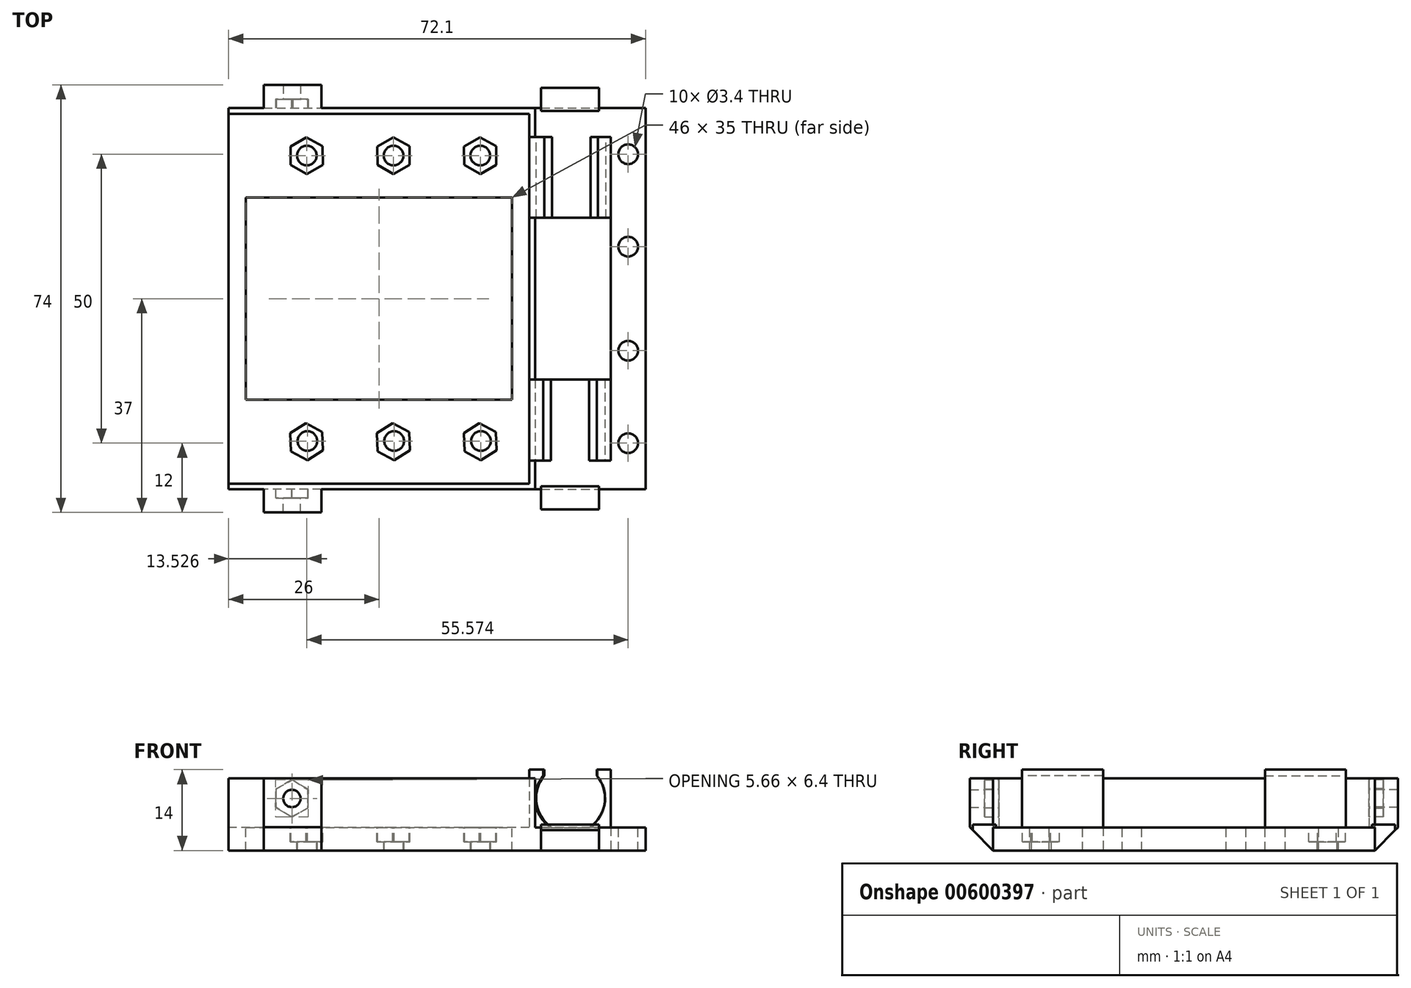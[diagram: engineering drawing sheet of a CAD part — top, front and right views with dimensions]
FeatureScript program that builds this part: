
annotation { "Feature Type Name" : "Feature", "Feature Type Description" : "" }
export const myFeature = defineFeature(function(context is Context, id is Id, definition is map)
    precondition{}
    {
        {
            var Q0;
            Q0=qCreatedBy(makeId("Top.planeOp"),FACE);
            var sketch = newSketch(context, id + "F0", { "sketchPlane" : qUnion([Q0])});
            skLineSegment(sketch, "E0.bottom", {"start": v(-26.5, 33) * mm, "end": v(26.5, 33) * mm});
            skLineSegment(sketch, "E0.top", {"start": v(-26.5, -33) * mm, "end": v(26.5, -33) * mm});
            skLineSegment(sketch, "E0.left", {"start": v(-26.5, 33) * mm, "end": v(-26.5, -33) * mm});
            skLineSegment(sketch, "E0.right", {"start": v(26.5, 33) * mm, "end": v(26.5, -33) * mm});
            skPoint(sketch, "E0.middle", {"position": v(0, 0) * mm});
            skSolve(sketch);
        }
        {
            var Q0;
            Q0=qSketchRegion(id+"F0",true);
            extrude(context, id + "F1", {"entities" : qUnion([Q0]), "depth" : 12.5 * mm});
        }
        {
            var Q0;
            Q0=makeQuery(id+"F1.opExtrude","SWEPT_FACE",FACE,{"disambiguationData":[OSD([sQuery(id+"F0.wireOp",EDGE,"E0.left")])]});
            var sketch = newSketch(context, id + "F2", { "sketchPlane" : qUnion([Q0])});
            skLineSegment(sketch, "E1.bottom", {"start": v(-32, 12.5) * mm, "end": v(32, 12.5) * mm});
            skLineSegment(sketch, "E1.top", {"start": v(-32, 4) * mm, "end": v(32, 4) * mm});
            skLineSegment(sketch, "E1.left", {"start": v(-32, 12.5) * mm, "end": v(-32, 4) * mm});
            skLineSegment(sketch, "E1.right", {"start": v(32, 12.5) * mm, "end": v(32, 4) * mm});
            skSolve(sketch);
        }
        {
            var Q0;
            Q0=qSketchRegion(id+"F2",true);
            extrude(context, id + "F3", {"entities" : qUnion([Q0]), "operationType" : NewBodyOperationType.REMOVE, "oppositeDirection" : true, "depth" : 52 * mm});
        }
        {
            var Q0;
            Q0=makeQuery(id+"F3.boolean.opBoolean","COPY",FACE,{"derivedFrom":makeQuery(id+"F3.opExtrude","SWEPT_FACE",FACE,{"disambiguationData":[OSD([sQuery(id+"F2.wireOp",EDGE,"E1.top")])]})});
            var sketch = newSketch(context, id + "F4", { "sketchPlane" : qUnion([Q0])});
            skLineSegment(sketch, "E2.bottom", {"start": v(-23.5, 17.5) * mm, "end": v(22.5, 17.5) * mm});
            skLineSegment(sketch, "E2.top", {"start": v(-23.5, -17.5) * mm, "end": v(22.5, -17.5) * mm});
            skLineSegment(sketch, "E2.left", {"start": v(-23.5, 17.5) * mm, "end": v(-23.5, -17.5) * mm});
            skLineSegment(sketch, "E2.right", {"start": v(22.5, 17.5) * mm, "end": v(22.5, -17.5) * mm});
            skSolve(sketch);
        }
        {
            var Q0;
            Q0=qSketchRegion(id+"F4",true);
            extrude(context, id + "F5", {"entities" : qUnion([Q0]), "operationType" : NewBodyOperationType.REMOVE, "oppositeDirection" : true, "depth" : 5 * mm, "offsetDistance" : 25 * mm});
        }
        {
            var Q0;
            Q0=makeQuery(id+"F1.opExtrude","SWEPT_FACE",FACE,{"disambiguationData":[OSD([sQuery(id+"F0.wireOp",EDGE,"E0.right")])]});
            var sketch = newSketch(context, id + "F6", { "sketchPlane" : qUnion([Q0])});
            skLineSegment(sketch, "E3.bottom", {"start": v(-28, 12.5) * mm, "end": v(-14, 12.5) * mm});
            skLineSegment(sketch, "E3.top", {"start": v(-28, 0) * mm, "end": v(-14, 0) * mm});
            skLineSegment(sketch, "E3.left", {"start": v(-28, 12.5) * mm, "end": v(-28, 0) * mm});
            skLineSegment(sketch, "E3.right", {"start": v(-14, 12.5) * mm, "end": v(-14, 0) * mm});
            skSolve(sketch);
        }
        {
            var Q0;
            Q0=qSketchRegion(id+"F6",true);
            extrude(context, id + "F7", {"entities" : qUnion([Q0]), "operationType" : NewBodyOperationType.REMOVE, "oppositeDirection" : true, "depth" : 1 * mm});
        }
        {
            var Q0;
            Q0=makeQuery(id+"F7.boolean.opBoolean","COPY",FACE,{"derivedFrom":makeQuery(id+"F7.opExtrude","CAP_FACE",FACE,{"disambiguationData":[OSD([sQuery(id+"F6.wireOp",EDGE,"E3.bottom"),sQuery(id+"F6.wireOp",EDGE,"E3.top"),sQuery(id+"F6.wireOp",EDGE,"E3.left"),sQuery(id+"F6.wireOp",EDGE,"E3.right")])],"isStart":false})});
            var sketch = newSketch(context, id + "F8", { "sketchPlane" : qUnion([Q0])});
            skLineSegment(sketch, "E4.bottom", {"start": v(-14, 0) * mm, "end": v(-28, 0) * mm});
            skLineSegment(sketch, "E4.top", {"start": v(-14, 14) * mm, "end": v(-28, 14) * mm});
            skLineSegment(sketch, "E4.left", {"start": v(-14, 0) * mm, "end": v(-14, 14) * mm});
            skLineSegment(sketch, "E4.right", {"start": v(-28, 0) * mm, "end": v(-28, 14) * mm});
            skSolve(sketch);
        }
        {
            var Q0;
            Q0=qSketchRegion(id+"F8",true);
            extrude(context, id + "F9", {"entities" : qUnion([Q0]), "operationType" : NewBodyOperationType.ADD, "depth" : 14.1 * mm});
        }
        {
            var Q0;
            Q0=makeQuery(id+"F9.opExtrude","SWEPT_FACE",FACE,{"disambiguationData":[OSD([sQuery(id+"F8.wireOp",EDGE,"E4.right")])]});
            var sketch = newSketch(context, id + "F10", { "sketchPlane" : qUnion([Q0])});
            skArc(sketch, "E5", {"start": v(27.89, 12.91) * mm, "mid": v(26.56, 8.16) * mm, "end": v(29.21, 4) * mm});
            skLineSegment(sketch, "E6", {"start": v(27.89, 14) * mm, "end": v(27.89, 12.91) * mm});
            skLineSegment(sketch, "E7", {"start": v(37.2, 12.91) * mm, "end": v(37.2, 14) * mm});
            skLineSegment(sketch, "E8", {"start": v(27.89, 14) * mm, "end": v(37.2, 14) * mm});
            skLineSegment(sketch, "E9", {"start": v(29.21, 4) * mm, "end": v(35.88, 4) * mm});
            skArc(sketch, "E10.trimOffspring", {"start": v(35.88, 4) * mm, "mid": v(38.53, 8.16) * mm, "end": v(37.2, 12.91) * mm});
            skSolve(sketch);
        }
        {
            var Q0;
            Q0=qSketchRegion(id+"F10",true);
            extrude(context, id + "F11", {"entities" : qUnion([Q0]), "operationType" : NewBodyOperationType.REMOVE, "oppositeDirection" : true, "depth" : 14 * mm});
        }
        {
            var Q0;
            {var subQ0=sQuery(id+"F0.wireOp",EDGE,"E0.bottom");var subQ1=sQuery(id+"F0.wireOp",EDGE,"E0.right");Q0=makeQuery(id+"F7.boolean.opBoolean","SPLIT",FACE,{"disambiguationData":[TD([makeQuery(id+"F1.opExtrude","SWEPT_FACE",FACE,{"disambiguationData":[OSD([subQ0])]})])],"derivedFrom":makeQuery(id+"F1.opExtrude","SWEPT_FACE",FACE,{"disambiguationData":[OSD([subQ1])]})});}
            var sketch = newSketch(context, id + "F12", { "sketchPlane" : qUnion([Q0])});
            skLineSegment(sketch, "E11.bottom", {"start": v(28, 0) * mm, "end": v(14, 0) * mm});
            skLineSegment(sketch, "E11.top", {"start": v(28, 14) * mm, "end": v(14, 14) * mm});
            skLineSegment(sketch, "E11.left", {"start": v(28, 0) * mm, "end": v(28, 14) * mm});
            skLineSegment(sketch, "E11.right", {"start": v(14, 0) * mm, "end": v(14, 14) * mm});
            skSolve(sketch);
        }
        {
            var Q0;
            Q0=qSketchRegion(id+"F12",true);
            var Q1;
            {var subQ3=sQuery(id+"F2.wireOp",EDGE,"E1.right");var subQ4=sQuery(id+"F2.wireOp",EDGE,"E1.top");var subQ7=sQuery(id+"F2.wireOp",EDGE,"E1.left");var subQ8=makeQuery(id+"F3.boolean.opBoolean","COPY",FACE,{"derivedFrom":makeQuery(id+"F3.opExtrude","CAP_FACE",FACE,{"disambiguationData":[OSD([sQuery(id+"F2.wireOp",EDGE,"E1.bottom"),subQ4,subQ7,subQ3])],"isStart":false})});Q1=makeQuery(id+"F9.boolean.opBoolean","MERGE",FACE,{"derivedFrom":[makeQuery(id+"F7.boolean.opBoolean","SPLIT",FACE,{"disambiguationData":[TD([makeQuery(id+"F3.boolean.opBoolean","COPY",FACE,{"derivedFrom":makeQuery(id+"F3.opExtrude","SWEPT_FACE",FACE,{"disambiguationData":[OSD([subQ7])]})})])],"derivedFrom":subQ8}),makeQuery(id+"F7.boolean.opBoolean","SPLIT",FACE,{"disambiguationData":[TD([makeQuery(id+"F3.boolean.opBoolean","COPY",FACE,{"derivedFrom":makeQuery(id+"F3.opExtrude","SWEPT_FACE",FACE,{"disambiguationData":[OSD([subQ3])]})})])],"derivedFrom":subQ8}),makeQuery(id+"F9.opExtrude","CAP_FACE",FACE,{"disambiguationData":[OSD([sQuery(id+"F8.wireOp",EDGE,"E4.bottom"),sQuery(id+"F8.wireOp",EDGE,"E4.top"),sQuery(id+"F8.wireOp",EDGE,"E4.left"),sQuery(id+"F8.wireOp",EDGE,"E4.right")])],"isStart":true})]});}
            extrude(context, id + "F13", {"entities" : qUnion([Q0]), "operationType" : NewBodyOperationType.ADD, "endBound" : BoundingType.UP_TO_SURFACE, "oppositeDirection" : true, "endBoundEntityFace" : qUnion([Q1]), "depth" : 25 * mm, "hasSecondDirection" : true, "secondDirectionOppositeDirection" : false, "secondDirectionDepth" : 13.1 * mm});
        }
        {
            var Q0;
            Q0=makeQuery(id+"F13.opExtrude","SWEPT_FACE",FACE,{"disambiguationData":[OSD([sQuery(id+"F12.wireOp",EDGE,"E11.left")])]});
            var sketch = newSketch(context, id + "F14", { "sketchPlane" : qUnion([Q0])});
            skArc(sketch, "E12", {"start": v(-37.37, 12.94) * mm, "mid": v(-38.72, 8.18) * mm, "end": v(-36.07, 4) * mm});
            skLineSegment(sketch, "E13", {"start": v(-36.07, 4) * mm, "end": v(-29.4, 4) * mm});
            skLineSegment(sketch, "E14", {"start": v(-37.37, 14) * mm, "end": v(-37.37, 12.94) * mm});
            skLineSegment(sketch, "E15", {"start": v(-28.1, 12.94) * mm, "end": v(-28.1, 14) * mm});
            skArc(sketch, "E16.trimOffspring", {"start": v(-29.4, 4) * mm, "mid": v(-26.75, 8.18) * mm, "end": v(-28.1, 12.94) * mm});
            skLineSegment(sketch, "E17", {"start": v(-37.37, 14) * mm, "end": v(-28.1, 14) * mm});
            skSolve(sketch);
        }
        {
            var Q0;
            Q0=qSketchRegion(id+"F14",true);
            extrude(context, id + "F15", {"entities" : qUnion([Q0]), "operationType" : NewBodyOperationType.REMOVE, "oppositeDirection" : true, "depth" : 14 * mm});
        }
        {
            var Q0;
            {var subQ0=sQuery(id+"F0.wireOp",EDGE,"E0.right");var subQ2=sQuery(id+"F0.wireOp",EDGE,"E0.top");Q0=makeQuery(id+"F7.boolean.opBoolean","SPLIT",FACE,{"disambiguationData":[TD([makeQuery(id+"F1.opExtrude","SWEPT_FACE",FACE,{"disambiguationData":[OSD([subQ2])]})])],"derivedFrom":makeQuery(id+"F1.opExtrude","SWEPT_FACE",FACE,{"disambiguationData":[OSD([subQ0])]})});}
            var sketch = newSketch(context, id + "F16", { "sketchPlane" : qUnion([Q0])});
            skLineSegment(sketch, "E18.bottom", {"start": v(-33, 4) * mm, "end": v(-28, 4) * mm});
            skLineSegment(sketch, "E18.top", {"start": v(-33, 0) * mm, "end": v(-28, 0) * mm});
            skLineSegment(sketch, "E18.left", {"start": v(-33, 4) * mm, "end": v(-33, 0) * mm});
            skLineSegment(sketch, "E18.right", {"start": v(-28, 4) * mm, "end": v(-28, 0) * mm});
            skSolve(sketch);
        }
        {
            var Q0;
            Q0=qSketchRegion(id+"F16",true);
            var Q1;
            Q1=makeQuery(id+"F9.opExtrude","CAP_FACE",FACE,{"disambiguationData":[OSD([sQuery(id+"F8.wireOp",EDGE,"E4.bottom"),sQuery(id+"F8.wireOp",EDGE,"E4.top"),sQuery(id+"F8.wireOp",EDGE,"E4.left"),sQuery(id+"F8.wireOp",EDGE,"E4.right")])],"isStart":false});
            extrude(context, id + "F17", {"entities" : qUnion([Q0]), "operationType" : NewBodyOperationType.ADD, "endBound" : BoundingType.UP_TO_SURFACE, "endBoundEntityFace" : qUnion([Q1]), "depth" : 25 * mm});
        }
        {
            var Q0;
            {var subQ0=sQuery(id+"F0.wireOp",EDGE,"E0.right");var subQ3=sQuery(id+"F0.wireOp",EDGE,"E0.bottom");var subQ6=makeQuery(id+"F1.opExtrude","SWEPT_FACE",FACE,{"disambiguationData":[OSD([subQ3])]});Q0=makeQuery(id+"F13.boolean.opBoolean","SPLIT",FACE,{"disambiguationData":[TD([subQ6])],"derivedFrom":makeQuery(id+"F7.boolean.opBoolean","SPLIT",FACE,{"disambiguationData":[TD([subQ6])],"derivedFrom":makeQuery(id+"F1.opExtrude","SWEPT_FACE",FACE,{"disambiguationData":[OSD([subQ0])]})})});}
            var sketch = newSketch(context, id + "F18", { "sketchPlane" : qUnion([Q0])});
            skLineSegment(sketch, "E19.bottom", {"start": v(28, 4) * mm, "end": v(33, 4) * mm});
            skLineSegment(sketch, "E19.top", {"start": v(28, 0) * mm, "end": v(33, 0) * mm});
            skLineSegment(sketch, "E19.left", {"start": v(28, 4) * mm, "end": v(28, 0) * mm});
            skLineSegment(sketch, "E19.right", {"start": v(33, 4) * mm, "end": v(33, 0) * mm});
            skSolve(sketch);
        }
        {
            var Q0;
            Q0=qSketchRegion(id+"F18",true);
            var Q1;
            Q1=makeQuery(id+"F13.opExtrude","CAP_FACE",FACE,{"disambiguationData":[OSD([sQuery(id+"F12.wireOp",EDGE,"E11.bottom"),sQuery(id+"F12.wireOp",EDGE,"E11.top"),sQuery(id+"F12.wireOp",EDGE,"E11.left"),sQuery(id+"F12.wireOp",EDGE,"E11.right")])],"isStart":true});
            extrude(context, id + "F19", {"entities" : qUnion([Q0]), "operationType" : NewBodyOperationType.ADD, "endBound" : BoundingType.UP_TO_SURFACE, "endBoundEntityFace" : qUnion([Q1]), "depth" : 25 * mm});
        }
        {
            var Q0;
            {var subQ0=sQuery(id+"F8.wireOp",EDGE,"E4.right");var subQ1=sQuery(id+"F8.wireOp",EDGE,"E4.left");var subQ2=sQuery(id+"F8.wireOp",EDGE,"E4.top");var subQ3=sQuery(id+"F8.wireOp",EDGE,"E4.bottom");Q0=makeQuery(id+"F17.boolean.opBoolean","MERGE",FACE,{"derivedFrom":[makeQuery(id+"F9.opExtrude","CAP_FACE",FACE,{"disambiguationData":[OSD([subQ3,subQ2,subQ1,subQ0])],"isStart":false}),makeQuery(id+"F17.opExtrude","CAP_FACE",FACE,{"disambiguationData":[OSD([subQ3,subQ2,subQ1,subQ0])],"isStart":false})]});}
            var sketch = newSketch(context, id + "F20", { "sketchPlane" : qUnion([Q0])});
            skLineSegment(sketch, "E20.bottom", {"start": v(-33, 4) * mm, "end": v(33, 4) * mm});
            skLineSegment(sketch, "E20.top", {"start": v(-33, 0) * mm, "end": v(33, 0) * mm});
            skLineSegment(sketch, "E20.left", {"start": v(-33, 4) * mm, "end": v(-33, 0) * mm});
            skLineSegment(sketch, "E20.right", {"start": v(33, 4) * mm, "end": v(33, 0) * mm});
            skSolve(sketch);
        }
        {
            var Q0;
            Q0=qSketchRegion(id+"F20",true);
            extrude(context, id + "F21", {"entities" : qUnion([Q0]), "operationType" : NewBodyOperationType.ADD, "depth" : 6 * mm});
        }
        {
            var Q0;
            Q0=makeQuery(id+"F21.boolean.opBoolean","MERGE",FACE,{"derivedFrom":[makeQuery(id+"F17.boolean.opBoolean","MERGE",FACE,{"derivedFrom":[makeQuery(id+"F1.opExtrude","SWEPT_FACE",FACE,{"disambiguationData":[OSD([sQuery(id+"F0.wireOp",EDGE,"E0.top")])]}),makeQuery(id+"F17.opExtrude","SWEPT_FACE",FACE,{"disambiguationData":[OSD([sQuery(id+"F16.wireOp",EDGE,"E18.left")])]})]}),makeQuery(id+"F21.opExtrude","SWEPT_FACE",FACE,{"disambiguationData":[OSD([sQuery(id+"F20.wireOp",EDGE,"E20.left")])]})]});
            var sketch = newSketch(context, id + "F22", { "sketchPlane" : qUnion([Q0])});
            skLineSegment(sketch, "E21.bottom", {"start": v(37.55, 0) * mm, "end": v(27.55, 0) * mm});
            skLineSegment(sketch, "E21.top", {"start": v(37.55, 4.5) * mm, "end": v(27.55, 4.5) * mm});
            skLineSegment(sketch, "E21.left", {"start": v(37.55, 0) * mm, "end": v(37.55, 4.5) * mm});
            skLineSegment(sketch, "E21.right", {"start": v(27.55, 0) * mm, "end": v(27.55, 4.5) * mm});
            skSolve(sketch);
        }
        {
            var Q0;
            Q0=qSketchRegion(id+"F22",true);
            extrude(context, id + "F23", {"entities" : qUnion([Q0]), "operationType" : NewBodyOperationType.ADD, "oppositeDirection" : true, "depth" : .5 * mm, "hasSecondDirection" : true, "secondDirectionOppositeDirection" : false, "secondDirectionDepth" : 3.5 * mm});
        }
        {
            var Q0;
            Q0=makeQuery(id+"F23.opExtrude","SWEPT_FACE",FACE,{"disambiguationData":[OSD([sQuery(id+"F22.wireOp",EDGE,"E21.left")])]});
            var sketch = newSketch(context, id + "F24", { "sketchPlane" : qUnion([Q0])});
            skLineSegment(sketch, "E22", {"start": v(-33, 0) * mm, "end": v(-36.5, 3.5) * mm});
            skLineSegment(sketch, "E23", {"start": v(-36.5, 3.5) * mm, "end": v(-36.5, 0) * mm});
            skLineSegment(sketch, "E24", {"start": v(-36.5, 0) * mm, "end": v(-33, 0) * mm});
            skSolve(sketch);
        }
        {
            var Q0;
            Q0=qSketchRegion(id+"F24",true);
            extrude(context, id + "F25", {"entities" : qUnion([Q0]), "operationType" : NewBodyOperationType.REMOVE, "oppositeDirection" : true, "depth" : 10 * mm});
        }
        {
            var Q0;
            {var subQ1=sQuery(id+"F0.wireOp",EDGE,"E0.left");var subQ2=sQuery(id+"F0.wireOp",EDGE,"E0.top");Q0=makeQuery(id+"F23.boolean.opBoolean","SPLIT",FACE,{"disambiguationData":[TD([makeQuery(id+"F1.opExtrude","SWEPT_FACE",FACE,{"disambiguationData":[OSD([subQ1])]})])],"derivedFrom":makeQuery(id+"F21.boolean.opBoolean","MERGE",FACE,{"derivedFrom":[makeQuery(id+"F17.boolean.opBoolean","MERGE",FACE,{"derivedFrom":[makeQuery(id+"F1.opExtrude","SWEPT_FACE",FACE,{"disambiguationData":[OSD([subQ2])]}),makeQuery(id+"F17.opExtrude","SWEPT_FACE",FACE,{"disambiguationData":[OSD([sQuery(id+"F16.wireOp",EDGE,"E18.left")])]})]}),makeQuery(id+"F21.opExtrude","SWEPT_FACE",FACE,{"disambiguationData":[OSD([sQuery(id+"F20.wireOp",EDGE,"E20.left")])]})]})});}
            var sketch = newSketch(context, id + "F26", { "sketchPlane" : qUnion([Q0])});
            skLineSegment(sketch, "E25.bottom", {"start": v(-20.45, 12.5) * mm, "end": v(-10.45, 12.5) * mm});
            skLineSegment(sketch, "E25.top", {"start": v(-20.45, 0) * mm, "end": v(-10.45, 0) * mm});
            skLineSegment(sketch, "E25.left", {"start": v(-20.45, 12.5) * mm, "end": v(-20.45, 0) * mm});
            skLineSegment(sketch, "E25.right", {"start": v(-10.45, 12.5) * mm, "end": v(-10.45, 0) * mm});
            skSolve(sketch);
        }
        {
            var Q0;
            Q0=qSketchRegion(id+"F26",true);
            extrude(context, id + "F27", {"entities" : qUnion([Q0]), "operationType" : NewBodyOperationType.ADD, "depth" : 4 * mm});
        }
        {
            var Q0;
            Q0=makeQuery(id+"F27.opExtrude","SWEPT_FACE",FACE,{"disambiguationData":[OSD([sQuery(id+"F26.wireOp",EDGE,"E25.left")])]});
            var sketch = newSketch(context, id + "F28", { "sketchPlane" : qUnion([Q0])});
            skLineSegment(sketch, "E26", {"start": v(37, 0) * mm, "end": v(37, 4.04) * mm});
            skLineSegment(sketch, "E27", {"start": v(37, 4.04) * mm, "end": v(33, 0) * mm});
            skLineSegment(sketch, "E28", {"start": v(33, 0) * mm, "end": v(37, 0) * mm});
            skSolve(sketch);
        }
        {
            var Q0;
            Q0=qSketchRegion(id+"F28",true);
            var Q1;
            Q1=makeQuery(id+"F27.opExtrude","SWEPT_FACE",FACE,{"disambiguationData":[OSD([sQuery(id+"F26.wireOp",EDGE,"E25.right")])]});
            extrude(context, id + "F29", {"entities" : qUnion([Q0]), "operationType" : NewBodyOperationType.REMOVE, "endBound" : BoundingType.UP_TO_SURFACE, "oppositeDirection" : true, "endBoundEntityFace" : qUnion([Q1]), "depth" : 25 * mm});
        }
        {
            var Q0;
            Q0=makeQuery(id+"F21.boolean.opBoolean","MERGE",FACE,{"derivedFrom":[makeQuery(id+"F19.boolean.opBoolean","MERGE",FACE,{"derivedFrom":[makeQuery(id+"F1.opExtrude","SWEPT_FACE",FACE,{"disambiguationData":[OSD([sQuery(id+"F0.wireOp",EDGE,"E0.bottom")])]}),makeQuery(id+"F19.opExtrude","SWEPT_FACE",FACE,{"disambiguationData":[OSD([sQuery(id+"F18.wireOp",EDGE,"E19.right")])]})]}),makeQuery(id+"F21.opExtrude","SWEPT_FACE",FACE,{"disambiguationData":[OSD([sQuery(id+"F20.wireOp",EDGE,"E20.right")])]})]});
            var sketch = newSketch(context, id + "F30", { "sketchPlane" : qUnion([Q0])});
            skLineSegment(sketch, "E29.bottom", {"start": v(-27.55, 0) * mm, "end": v(-37.55, 0) * mm});
            skLineSegment(sketch, "E29.top", {"start": v(-27.55, 4.5) * mm, "end": v(-37.55, 4.5) * mm});
            skLineSegment(sketch, "E29.left", {"start": v(-27.55, 0) * mm, "end": v(-27.55, 4.5) * mm});
            skLineSegment(sketch, "E29.right", {"start": v(-37.55, 0) * mm, "end": v(-37.55, 4.5) * mm});
            skSolve(sketch);
        }
        {
            var Q0;
            Q0=qSketchRegion(id+"F30",true);
            extrude(context, id + "F31", {"entities" : qUnion([Q0]), "operationType" : NewBodyOperationType.ADD, "oppositeDirection" : true, "depth" : 0.5 * mm, "hasSecondDirection" : true, "secondDirectionOppositeDirection" : false, "secondDirectionDepth" : 3.5 * mm});
        }
        {
            var Q0;
            Q0=makeQuery(id+"F31.opExtrude","SWEPT_FACE",FACE,{"disambiguationData":[OSD([sQuery(id+"F30.wireOp",EDGE,"E29.right")])]});
            var sketch = newSketch(context, id + "F32", { "sketchPlane" : qUnion([Q0])});
            skLineSegment(sketch, "E30", {"start": v(33, 0) * mm, "end": v(36.5, 3.5) * mm});
            skLineSegment(sketch, "E31", {"start": v(36.5, 3.5) * mm, "end": v(36.5, 0) * mm});
            skLineSegment(sketch, "E32", {"start": v(36.5, 0) * mm, "end": v(33, 0) * mm});
            skSolve(sketch);
        }
        {
            var Q0;
            Q0=qSketchRegion(id+"F32",true);
            var Q1;
            Q1=makeQuery(id+"F31.opExtrude","SWEPT_FACE",FACE,{"disambiguationData":[OSD([sQuery(id+"F30.wireOp",EDGE,"E29.left")])]});
            extrude(context, id + "F33", {"entities" : qUnion([Q0]), "operationType" : NewBodyOperationType.REMOVE, "endBound" : BoundingType.UP_TO_SURFACE, "oppositeDirection" : true, "endBoundEntityFace" : qUnion([Q1]), "depth" : 25 * mm});
        }
        {
            var Q0;
            {var subQ1=sQuery(id+"F0.wireOp",EDGE,"E0.left");var subQ3=sQuery(id+"F0.wireOp",EDGE,"E0.bottom");Q0=makeQuery(id+"F31.boolean.opBoolean","SPLIT",FACE,{"disambiguationData":[TD([makeQuery(id+"F1.opExtrude","SWEPT_FACE",FACE,{"disambiguationData":[OSD([subQ1])]})])],"derivedFrom":makeQuery(id+"F21.boolean.opBoolean","MERGE",FACE,{"derivedFrom":[makeQuery(id+"F19.boolean.opBoolean","MERGE",FACE,{"derivedFrom":[makeQuery(id+"F1.opExtrude","SWEPT_FACE",FACE,{"disambiguationData":[OSD([subQ3])]}),makeQuery(id+"F19.opExtrude","SWEPT_FACE",FACE,{"disambiguationData":[OSD([sQuery(id+"F18.wireOp",EDGE,"E19.right")])]})]}),makeQuery(id+"F21.opExtrude","SWEPT_FACE",FACE,{"disambiguationData":[OSD([sQuery(id+"F20.wireOp",EDGE,"E20.right")])]})]})});}
            var sketch = newSketch(context, id + "F34", { "sketchPlane" : qUnion([Q0])});
            skLineSegment(sketch, "E33.bottom", {"start": v(10.45, 12.5) * mm, "end": v(20.45, 12.5) * mm});
            skLineSegment(sketch, "E33.top", {"start": v(10.45, 0) * mm, "end": v(20.45, 0) * mm});
            skLineSegment(sketch, "E33.left", {"start": v(10.45, 12.5) * mm, "end": v(10.45, 0) * mm});
            skLineSegment(sketch, "E33.right", {"start": v(20.45, 12.5) * mm, "end": v(20.45, 0) * mm});
            skSolve(sketch);
        }
        {
            var Q0;
            Q0=qSketchRegion(id+"F34",true);
            extrude(context, id + "F35", {"entities" : qUnion([Q0]), "operationType" : NewBodyOperationType.ADD, "depth" : 4 * mm});
        }
        {
            var Q0;
            Q0=makeQuery(id+"F35.opExtrude","SWEPT_FACE",FACE,{"disambiguationData":[OSD([sQuery(id+"F34.wireOp",EDGE,"E33.left")])]});
            var sketch = newSketch(context, id + "F36", { "sketchPlane" : qUnion([Q0])});
            skLineSegment(sketch, "E34", {"start": v(33, 0) * mm, "end": v(37, 4) * mm});
            skLineSegment(sketch, "E35", {"start": v(37, 4) * mm, "end": v(37, 0) * mm});
            skLineSegment(sketch, "E36", {"start": v(37, 0) * mm, "end": v(33, 0) * mm});
            skSolve(sketch);
        }
        {
            var Q0;
            Q0=qSketchRegion(id+"F36",true);
            var Q1;
            Q1=makeQuery(id+"F35.opExtrude","SWEPT_FACE",FACE,{"disambiguationData":[OSD([sQuery(id+"F34.wireOp",EDGE,"E33.right")])]});
            extrude(context, id + "F37", {"entities" : qUnion([Q0]), "operationType" : NewBodyOperationType.REMOVE, "endBound" : BoundingType.UP_TO_SURFACE, "oppositeDirection" : true, "endBoundEntityFace" : qUnion([Q1]), "depth" : 25 * mm});
        }
        {
            var Q0;
            Q0=makeQuery(id+"F3.boolean.opBoolean","COPY",FACE,{"derivedFrom":makeQuery(id+"F3.opExtrude","SWEPT_FACE",FACE,{"disambiguationData":[OSD([sQuery(id+"F2.wireOp",EDGE,"E1.right")])]})});
            var sketch = newSketch(context, id + "F38", { "sketchPlane" : qUnion([Q0])});
            skCircle(sketch, "E37.cCircle", {"center": v(15.55, 9) * mm, "radius": 2.77 * mm, "construction": true});
            skLineSegment(sketch, "E37.0", {"start": v(12.8, 10.62) * mm, "end": v(15.57, 12.2) * mm});
            skLineSegment(sketch, "E37.1", {"start": v(15.57, 12.2) * mm, "end": v(18.33, 10.58) * mm});
            skLineSegment(sketch, "E37.2", {"start": v(18.33, 10.58) * mm, "end": v(18.3, 7.38) * mm});
            skLineSegment(sketch, "E37.3", {"start": v(18.3, 7.38) * mm, "end": v(15.53, 5.8) * mm});
            skLineSegment(sketch, "E37.4", {"start": v(15.53, 5.8) * mm, "end": v(12.77, 7.42) * mm});
            skLineSegment(sketch, "E37.5", {"start": v(12.77, 7.42) * mm, "end": v(12.8, 10.62) * mm});
            skPoint(sketch, "E37.0.midPoint", {"position": v(14.18, 11.41) * mm});
            skSolve(sketch);
        }
        {
            var Q0;
            Q0=qSketchRegion(id+"F38",true);
            extrude(context, id + "F39", {"entities" : qUnion([Q0]), "operationType" : NewBodyOperationType.REMOVE, "oppositeDirection" : true, "depth" : 2.5 * mm});
        }
        {
            var Q0;
            Q0=makeQuery(id+"F3.boolean.opBoolean","COPY",FACE,{"derivedFrom":makeQuery(id+"F3.opExtrude","SWEPT_FACE",FACE,{"disambiguationData":[OSD([sQuery(id+"F2.wireOp",EDGE,"E1.right")])]})});
            var sketch = newSketch(context, id + "F40", { "sketchPlane" : qUnion([Q0])});
            skCircle(sketch, "E38", {"center": v(15.55, 9) * mm, "radius": 1.5 * mm});
            skSolve(sketch);
        }
        {
            var Q0;
            Q0=qSketchRegion(id+"F40",true);
            extrude(context, id + "F41", {"entities" : qUnion([Q0]), "operationType" : NewBodyOperationType.REMOVE, "oppositeDirection" : true, "depth" : 6 * mm});
        }
        {
            var Q0;
            Q0=makeQuery(id+"F3.boolean.opBoolean","COPY",FACE,{"derivedFrom":makeQuery(id+"F3.opExtrude","SWEPT_FACE",FACE,{"disambiguationData":[OSD([sQuery(id+"F2.wireOp",EDGE,"E1.left")])]})});
            var sketch = newSketch(context, id + "F42", { "sketchPlane" : qUnion([Q0])});
            skCircle(sketch, "E39.cCircle", {"center": v(-15.55, 9) * mm, "radius": 2.77 * mm, "construction": true});
            skLineSegment(sketch, "E39.0", {"start": v(-12.84, 7.3) * mm, "end": v(-15.67, 5.8) * mm});
            skLineSegment(sketch, "E39.1", {"start": v(-15.67, 5.8) * mm, "end": v(-18.38, 7.5) * mm});
            skLineSegment(sketch, "E39.2", {"start": v(-18.38, 7.5) * mm, "end": v(-18.26, 10.7) * mm});
            skLineSegment(sketch, "E39.3", {"start": v(-18.26, 10.7) * mm, "end": v(-15.43, 12.2) * mm});
            skLineSegment(sketch, "E39.4", {"start": v(-15.43, 12.2) * mm, "end": v(-12.72, 10.5) * mm});
            skLineSegment(sketch, "E39.5", {"start": v(-12.72, 10.5) * mm, "end": v(-12.84, 7.3) * mm});
            skPoint(sketch, "E39.0.midPoint", {"position": v(-14.25, 6.55) * mm});
            skSolve(sketch);
        }
        {
            var Q0;
            Q0=qSketchRegion(id+"F42",true);
            extrude(context, id + "F43", {"entities" : qUnion([Q0]), "operationType" : NewBodyOperationType.REMOVE, "oppositeDirection" : true, "depth" : 2.5 * mm});
        }
        {
            var Q0;
            Q0=makeQuery(id+"F3.boolean.opBoolean","COPY",FACE,{"derivedFrom":makeQuery(id+"F3.opExtrude","SWEPT_FACE",FACE,{"disambiguationData":[OSD([sQuery(id+"F2.wireOp",EDGE,"E1.left")])]})});
            var sketch = newSketch(context, id + "F44", { "sketchPlane" : qUnion([Q0])});
            skCircle(sketch, "E40", {"center": v(-15.55, 9) * mm, "radius": 1.5 * mm});
            skSolve(sketch);
        }
        {
            var Q0;
            Q0=qSketchRegion(id+"F44",true);
            extrude(context, id + "F45", {"entities" : qUnion([Q0]), "operationType" : NewBodyOperationType.REMOVE, "oppositeDirection" : true, "depth" : 6 * mm});
        }
        {
            var Q0;
            Q0=makeQuery(id+"F21.boolean.opBoolean","MERGE",FACE,{"derivedFrom":[makeQuery(id+"F17.boolean.opBoolean","MERGE",FACE,{"derivedFrom":[makeQuery(id+"F11.boolean.opBoolean","COPY",FACE,{"derivedFrom":makeQuery(id+"F11.opExtrude","SWEPT_FACE",FACE,{"disambiguationData":[OSD([sQuery(id+"F10.wireOp",EDGE,"E9")])]})}),makeQuery(id+"F17.opExtrude","SWEPT_FACE",FACE,{"disambiguationData":[OSD([sQuery(id+"F16.wireOp",EDGE,"E18.bottom")])]})]}),makeQuery(id+"F19.boolean.opBoolean","MERGE",FACE,{"derivedFrom":[makeQuery(id+"F15.boolean.opBoolean","COPY",FACE,{"derivedFrom":makeQuery(id+"F15.opExtrude","SWEPT_FACE",FACE,{"disambiguationData":[OSD([sQuery(id+"F14.wireOp",EDGE,"E13")])]})}),makeQuery(id+"F19.opExtrude","SWEPT_FACE",FACE,{"disambiguationData":[OSD([sQuery(id+"F18.wireOp",EDGE,"E19.bottom")])]})]}),makeQuery(id+"F21.opExtrude","SWEPT_FACE",FACE,{"disambiguationData":[OSD([sQuery(id+"F20.wireOp",EDGE,"E20.bottom")])]})]});
            var sketch = newSketch(context, id + "F46", { "sketchPlane" : qUnion([Q0])});
            skCircle(sketch, "E41", {"center": v(42.6, -25) * mm, "radius": 1.7 * mm});
            skCircle(sketch, "E42", {"center": v(42.6, -9) * mm, "radius": 1.7 * mm});
            skCircle(sketch, "E43", {"center": v(42.6, 9) * mm, "radius": 1.7 * mm});
            skCircle(sketch, "E44", {"center": v(42.6, 25) * mm, "radius": 1.7 * mm});
            skSolve(sketch);
        }
        {
            var Q0;
            Q0=qSketchRegion(id+"F46",true);
            extrude(context, id + "F47", {"entities" : qUnion([Q0]), "operationType" : NewBodyOperationType.REMOVE, "oppositeDirection" : true, "depth" : 5 * mm});
        }
        {
            var Q0;
            Q0=makeQuery(id+"F3.boolean.opBoolean","COPY",FACE,{"derivedFrom":makeQuery(id+"F3.opExtrude","SWEPT_FACE",FACE,{"disambiguationData":[OSD([sQuery(id+"F2.wireOp",EDGE,"E1.top")])]})});
            var sketch = newSketch(context, id + "F48", { "sketchPlane" : qUnion([Q0])});
            skCircle(sketch, "E45.cCircle", {"center": v(-13, 24.75) * mm, "radius": 2.77 * mm, "construction": true});
            skLineSegment(sketch, "E45.0", {"start": v(-10.22, 23.17) * mm, "end": v(-12.97, 21.55) * mm});
            skLineSegment(sketch, "E45.1", {"start": v(-12.97, 21.55) * mm, "end": v(-15.76, 23.13) * mm});
            skLineSegment(sketch, "E45.2", {"start": v(-15.76, 23.13) * mm, "end": v(-15.78, 26.33) * mm});
            skLineSegment(sketch, "E45.3", {"start": v(-15.78, 26.33) * mm, "end": v(-13.03, 27.95) * mm});
            skLineSegment(sketch, "E45.4", {"start": v(-13.03, 27.95) * mm, "end": v(-10.24, 26.37) * mm});
            skLineSegment(sketch, "E45.5", {"start": v(-10.24, 26.37) * mm, "end": v(-10.22, 23.17) * mm});
            skPoint(sketch, "E45.0.midPoint", {"position": v(-11.6, 22.36) * mm});
            skCircle(sketch, "E46.cCircle", {"center": v(2, 24.75) * mm, "radius": 2.77 * mm, "construction": true});
            skLineSegment(sketch, "E46.0", {"start": v(4.78, 23.17) * mm, "end": v(2.03, 21.55) * mm});
            skLineSegment(sketch, "E46.1", {"start": v(2.03, 21.55) * mm, "end": v(-0.76, 23.13) * mm});
            skLineSegment(sketch, "E46.2", {"start": v(-0.76, 23.13) * mm, "end": v(-0.78, 26.33) * mm});
            skLineSegment(sketch, "E46.3", {"start": v(-0.78, 26.33) * mm, "end": v(1.97, 27.95) * mm});
            skLineSegment(sketch, "E46.4", {"start": v(1.97, 27.95) * mm, "end": v(4.76, 26.37) * mm});
            skLineSegment(sketch, "E46.5", {"start": v(4.76, 26.37) * mm, "end": v(4.78, 23.17) * mm});
            skPoint(sketch, "E46.0.midPoint", {"position": v(3.4, 22.36) * mm});
            skCircle(sketch, "E47.cCircle", {"center": v(17, 24.75) * mm, "radius": 2.77 * mm, "construction": true});
            skLineSegment(sketch, "E47.0", {"start": v(19.78, 23.17) * mm, "end": v(17.03, 21.55) * mm});
            skLineSegment(sketch, "E47.1", {"start": v(17.03, 21.55) * mm, "end": v(14.24, 23.13) * mm});
            skLineSegment(sketch, "E47.2", {"start": v(14.24, 23.13) * mm, "end": v(14.22, 26.33) * mm});
            skLineSegment(sketch, "E47.3", {"start": v(14.22, 26.33) * mm, "end": v(16.97, 27.95) * mm});
            skLineSegment(sketch, "E47.4", {"start": v(16.97, 27.95) * mm, "end": v(19.76, 26.37) * mm});
            skLineSegment(sketch, "E47.5", {"start": v(19.76, 26.37) * mm, "end": v(19.78, 23.17) * mm});
            skPoint(sketch, "E47.0.midPoint", {"position": v(18.4, 22.36) * mm});
            skCircle(sketch, "E48.cCircle", {"center": v(-13, -24.75) * mm, "radius": 2.77 * mm, "construction": true});
            skLineSegment(sketch, "E48.0", {"start": v(-10.17, -26.24) * mm, "end": v(-12.87, -27.95) * mm});
            skLineSegment(sketch, "E48.1", {"start": v(-12.87, -27.95) * mm, "end": v(-15.7, -26.46) * mm});
            skLineSegment(sketch, "E48.2", {"start": v(-15.7, -26.46) * mm, "end": v(-15.83, -23.26) * mm});
            skLineSegment(sketch, "E48.3", {"start": v(-15.83, -23.26) * mm, "end": v(-13.13, -21.55) * mm});
            skLineSegment(sketch, "E48.4", {"start": v(-13.13, -21.55) * mm, "end": v(-10.3, -23.04) * mm});
            skLineSegment(sketch, "E48.5", {"start": v(-10.3, -23.04) * mm, "end": v(-10.17, -26.24) * mm});
            skPoint(sketch, "E48.0.midPoint", {"position": v(-11.52, -27.1) * mm});
            skCircle(sketch, "E49.cCircle", {"center": v(2, -24.75) * mm, "radius": 2.77 * mm, "construction": true});
            skLineSegment(sketch, "E49.0", {"start": v(4.83, -26.24) * mm, "end": v(2.13, -27.95) * mm});
            skLineSegment(sketch, "E49.1", {"start": v(2.13, -27.95) * mm, "end": v(-0.7, -26.46) * mm});
            skLineSegment(sketch, "E49.2", {"start": v(-0.7, -26.46) * mm, "end": v(-0.83, -23.26) * mm});
            skLineSegment(sketch, "E49.3", {"start": v(-0.83, -23.26) * mm, "end": v(1.87, -21.55) * mm});
            skLineSegment(sketch, "E49.4", {"start": v(1.87, -21.55) * mm, "end": v(4.7, -23.04) * mm});
            skLineSegment(sketch, "E49.5", {"start": v(4.7, -23.04) * mm, "end": v(4.83, -26.24) * mm});
            skPoint(sketch, "E49.0.midPoint", {"position": v(3.48, -27.1) * mm});
            skCircle(sketch, "E50.cCircle", {"center": v(17, -24.75) * mm, "radius": 2.77 * mm, "construction": true});
            skLineSegment(sketch, "E50.0", {"start": v(19.83, -26.24) * mm, "end": v(17.13, -27.95) * mm});
            skLineSegment(sketch, "E50.1", {"start": v(17.13, -27.95) * mm, "end": v(14.3, -26.46) * mm});
            skLineSegment(sketch, "E50.2", {"start": v(14.3, -26.46) * mm, "end": v(14.17, -23.26) * mm});
            skLineSegment(sketch, "E50.3", {"start": v(14.17, -23.26) * mm, "end": v(16.87, -21.55) * mm});
            skLineSegment(sketch, "E50.4", {"start": v(16.87, -21.55) * mm, "end": v(19.7, -23.04) * mm});
            skLineSegment(sketch, "E50.5", {"start": v(19.7, -23.04) * mm, "end": v(19.83, -26.24) * mm});
            skPoint(sketch, "E50.0.midPoint", {"position": v(18.48, -27.1) * mm});
            skSolve(sketch);
        }
        {
            var Q0;
            Q0=qSketchRegion(id+"F48",true);
            extrude(context, id + "F49", {"entities" : qUnion([Q0]), "operationType" : NewBodyOperationType.REMOVE, "oppositeDirection" : true, "depth" : 2.5 * mm});
        }
        {
            var Q0;
            Q0=makeQuery(id+"F3.boolean.opBoolean","COPY",FACE,{"derivedFrom":makeQuery(id+"F3.opExtrude","SWEPT_FACE",FACE,{"disambiguationData":[OSD([sQuery(id+"F2.wireOp",EDGE,"E1.top")])]})});
            var sketch = newSketch(context, id + "F50", { "sketchPlane" : qUnion([Q0])});
            skCircle(sketch, "E51", {"center": v(-12.97, 24.77) * mm, "radius": 1.7 * mm});
            skPoint(sketch, "E51.centerSnap0", {"position": v(-10.23, 24.77) * mm});
            skPoint(sketch, "E51.perimeterSnap0", {"position": v(-14.4, 27.14) * mm});
            skPoint(sketch, "E51.perimeterSnap1", {"position": v(-10.23, 24.77) * mm});
            skCircle(sketch, "E52", {"center": v(2.03, 24.77) * mm, "radius": 1.7 * mm});
            skPoint(sketch, "E52.centerSnap0", {"position": v(4.77, 24.77) * mm});
            skCircle(sketch, "E53", {"center": v(17.03, 24.77) * mm, "radius": 1.7 * mm});
            skPoint(sketch, "E53.centerSnap0", {"position": v(19.77, 24.77) * mm});
            skPoint(sketch, "E53.perimeterSnap0", {"position": v(19.77, 24.77) * mm});
            skPoint(sketch, "E53.perimeterSnap1", {"position": v(15.63, 22.34) * mm});
            skCircle(sketch, "E54", {"center": v(17.13, -24.64) * mm, "radius": 1.7 * mm});
            skPoint(sketch, "E54.centerSnap0", {"position": v(19.77, -24.64) * mm});
            skCircle(sketch, "E55", {"center": v(2.13, -24.64) * mm, "radius": 1.7 * mm});
            skPoint(sketch, "E55.centerSnap0", {"position": v(4.77, -24.64) * mm});
            skCircle(sketch, "E56", {"center": v(-12.87, -24.64) * mm, "radius": 1.7 * mm});
            skPoint(sketch, "E56.centerSnap0", {"position": v(-10.23, -24.64) * mm});
            skSolve(sketch);
        }
        {
            var Q0;
            Q0=qSketchRegion(id+"F50",true);
            extrude(context, id + "F51", {"entities" : qUnion([Q0]), "operationType" : NewBodyOperationType.REMOVE, "oppositeDirection" : true, "depth" : 6 * mm});
        }
    });
